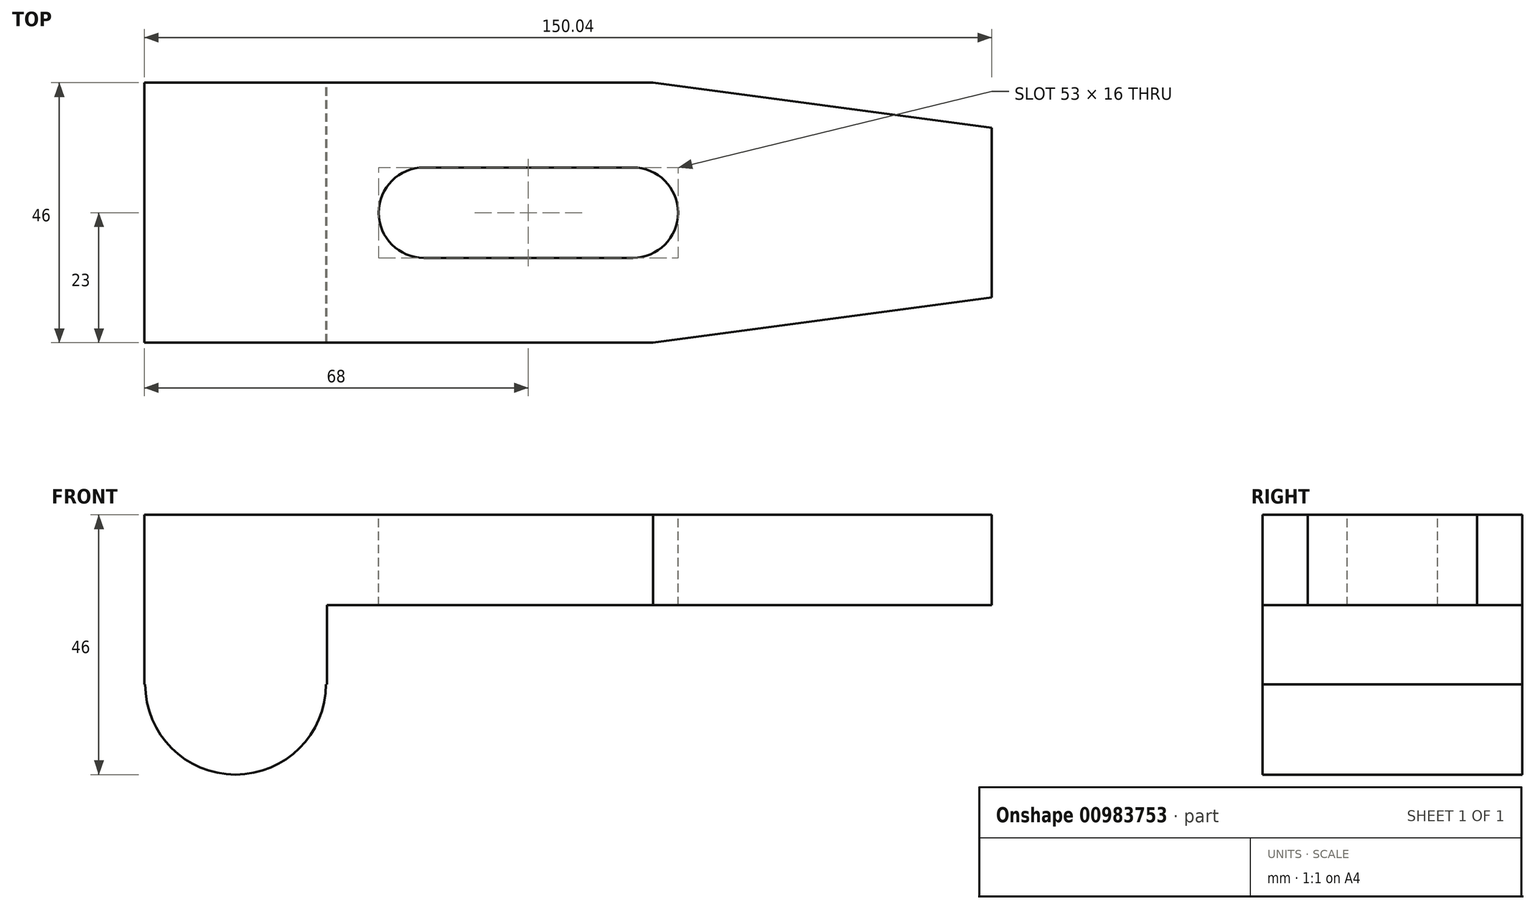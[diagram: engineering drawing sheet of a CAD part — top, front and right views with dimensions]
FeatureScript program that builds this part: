
annotation { "Feature Type Name" : "Feature", "Feature Type Description" : "" }
export const myFeature = defineFeature(function(context is Context, id is Id, definition is map)
    precondition{}
    {
        {
            var Q0;
            Q0=qCreatedBy(makeId("Front.planeOp"),FACE);
            var sketch = newSketch(context, id + "F0", { "sketchPlane" : qUnion([Q0])});
            skLineSegment(sketch, "E0.bottom", {"start": v(0, 0) * mm, "end": v(32.35, 0) * mm});
            skLineSegment(sketch, "E0.top", {"start": v(0, 30) * mm, "end": v(32.35, 30) * mm});
            skLineSegment(sketch, "E0.left", {"start": v(0, 0) * mm, "end": v(0, 30) * mm});
            skLineSegment(sketch, "E0.right", {"start": v(32.35, 0) * mm, "end": v(32.35, 30) * mm});
            skCircle(sketch, "E1", {"center": v(16.18, 0) * mm, "radius": 16 * mm});
            skLineSegment(sketch, "E2", {"start": v(0, 30) * mm, "end": v(67.96, 30) * mm});
            skLineSegment(sketch, "E3", {"start": v(67.96, 30) * mm, "end": v(104.97, 30) * mm});
            skLineSegment(sketch, "E4", {"start": v(0, 30) * mm, "end": v(45.02, 30) * mm});
            skLineSegment(sketch, "E5", {"start": v(45.02, 30) * mm, "end": v(45.02, 21.95) * mm});
            skLineSegment(sketch, "E6", {"start": v(0, 30) * mm, "end": v(150.04, 30) * mm});
            skLineSegment(sketch, "E7", {"start": v(150.04, 30) * mm, "end": v(150.04, 14) * mm});
            skLineSegment(sketch, "E8", {"start": v(150.04, 14) * mm, "end": v(32.35, 14) * mm});
            skSolve(sketch);
        }
        {
            var Q0;
            {var subQ0=sQuery(id+"F0.wireOp",EDGE,"E1");var subQ1=sQuery(id+"F0.wireOp",EDGE,"E0.bottom");var subQ2=makeQuery(id+"F0.imprint","INTERSECT",VERTEX,{"disambiguationData":[OD(0.0)],"derivedFrom":[subQ1,subQ0]});Q0=makeQuery(id+"F0.imprint","IMPRINT",FACE,{"disambiguationData":[TD([[makeQuery(id+"F0.imprint","IMPRINT",EDGE,{"disambiguationData":[TD([[subQ2,-1.0]])],"derivedFrom":subQ1}),-1.0]])]});}
            var Q1;
            {var subQ0=sQuery(id+"F0.wireOp",EDGE,"E1");var subQ1=sQuery(id+"F0.wireOp",EDGE,"E0.bottom");var subQ2=makeQuery(id+"F0.imprint","INTERSECT",VERTEX,{"disambiguationData":[OD(0.0)],"derivedFrom":[subQ1,subQ0]});Q1=makeQuery(id+"F0.imprint","IMPRINT",FACE,{"disambiguationData":[TD([[makeQuery(id+"F0.imprint","IMPRINT",EDGE,{"disambiguationData":[TD([[subQ2,-1.0]])],"derivedFrom":subQ1}),1.0]])]});}
            var Q2;
            {var subQ4=sQuery(id+"F0.wireOp",EDGE,"E0.left");Q2=makeQuery(id+"F0.imprint","IMPRINT",FACE,{"disambiguationData":[TD([[makeQuery(id+"F0.imprint","IMPRINT",EDGE,{"derivedFrom":subQ4}),-1.0]])]});}
            var Q3;
            {var subQ0=sQuery(id+"F0.wireOp",EDGE,"E7");Q3=makeQuery(id+"F0.imprint","IMPRINT",FACE,{"disambiguationData":[TD([[makeQuery(id+"F0.imprint","IMPRINT",EDGE,{"derivedFrom":subQ0}),-1.0]])]});}
            var Q4;
            Q4 = qSketchRegion(id + "F2", true);
            extrude(context, id + "F1", {"entities" : qUnion([Q0, Q1, Q2, Q3, Q4]), "depth" : 46 * mm, "offsetDistance" : 25 * mm});
        }
        {
            var Q0;
            Q0=makeQuery(id+"F1.opExtrude","SWEPT_FACE",FACE,{"disambiguationData":[OSD([sQuery(id+"F0.wireOp",EDGE,"E6")])]});
            var sketch = newSketch(context, id + "F2", { "sketchPlane" : qUnion([Q0])});
            skLineSegment(sketch, "E9", {"start": v(150.04, -46) * mm, "end": v(90.04, -46) * mm});
            skLineSegment(sketch, "E10", {"start": v(150.04, -46) * mm, "end": v(150.04, -38) * mm});
            skLineSegment(sketch, "E11", {"start": v(90.04, -46) * mm, "end": v(150.04, -38) * mm});
            skLineSegment(sketch, "E12", {"start": v(150.04, 0) * mm, "end": v(150.04, -8) * mm});
            skLineSegment(sketch, "E13", {"start": v(150.04, 0) * mm, "end": v(90.04, 0) * mm});
            skLineSegment(sketch, "E14", {"start": v(90.04, 0) * mm, "end": v(150.04, -8) * mm});
            skSolve(sketch);
        }
        {
            var Q0;
            Q0=makeQuery(id+"F2.imprint","IMPRINT",FACE,{"disambiguationData":[TD([[makeQuery(id+"F2.imprint","IMPRINT",EDGE,{"derivedFrom":sQuery(id+"F2.wireOp",EDGE,"E12")}),1.0]])]});
            var Q1;
            Q1=makeQuery(id+"F2.imprint","IMPRINT",FACE,{"disambiguationData":[TD([[makeQuery(id+"F2.imprint","IMPRINT",EDGE,{"derivedFrom":sQuery(id+"F2.wireOp",EDGE,"E9")}),1.0]])]});
            extrude(context, id + "F3", {"entities" : qUnion([Q0, Q1]), "operationType" : NewBodyOperationType.REMOVE, "oppositeDirection" : true, "depth" : 16 * mm, "offsetDistance" : 25 * mm});
        }
        {
            var Q0;
            Q0=makeQuery(id+"F1.opExtrude","SWEPT_FACE",FACE,{"disambiguationData":[OSD([sQuery(id+"F0.wireOp",EDGE,"E6")])]});
            var sketch = newSketch(context, id + "F4", { "sketchPlane" : qUnion([Q0])});
            skLineSegment(sketch, "E15", {"start": v(0, 0) * mm, "end": v(68, 0) * mm});
            skLineSegment(sketch, "E16", {"start": v(68, 0) * mm, "end": v(68, -15) * mm});
            skLineSegment(sketch, "E17.bottom", {"start": v(68, -31) * mm, "end": v(86.5, -31) * mm});
            skLineSegment(sketch, "E17.top", {"start": v(68, -15) * mm, "end": v(86.5, -15) * mm});
            skLineSegment(sketch, "E18", {"start": v(68, -15) * mm, "end": v(49.5, -15) * mm});
            skArc(sketch, "E19", {"start": v(49.5, -15) * mm, "mid": v(41.5, -23) * mm, "end": v(49.5, -31) * mm});
            skArc(sketch, "E20", {"start": v(86.5, -31) * mm, "mid": v(94.5, -23) * mm, "end": v(86.5, -15) * mm});
            skLineSegment(sketch, "E21", {"start": v(68, -31) * mm, "end": v(49.5, -31) * mm});
            skPoint(sketch, "E22.start.orphan", {"position": v(68, -46) * mm});
            skSolve(sketch);
        }
        {
            var Q0;
            Q0=makeQuery(id+"F4.imprint","IMPRINT",FACE,{"disambiguationData":[TD([[makeQuery(id+"F4.imprint","IMPRINT",EDGE,{"derivedFrom":sQuery(id+"F4.wireOp",EDGE,"E17.bottom")}),1.0]])]});
            extrude(context, id + "F5", {"entities" : qUnion([Q0]), "operationType" : NewBodyOperationType.REMOVE, "endBound" : BoundingType.THROUGH_ALL, "oppositeDirection" : true, "depth" : 25 * mm, "offsetDistance" : 25 * mm});
        }
    });
